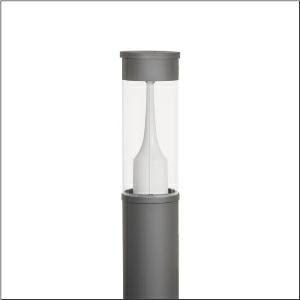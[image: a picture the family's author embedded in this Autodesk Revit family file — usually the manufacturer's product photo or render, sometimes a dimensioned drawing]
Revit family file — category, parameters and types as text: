
# Revit family: city-light_260_iq___p1_0a_5xa5295ff14h_c360
name_source: partatom
category: Lighting Fixtures
units: mm (PartAtom-declared; Revit-internal decimal feet)

## family parameters
Cut with Voids When Loaded = No
Host = Face
Light Source = No
Part Type = Normal
Room Calculation Point = No
Round Connector Dimension = Use Diameter
Shared = No

## types (1)
- --- (1 x LED, 1510 lm, 10.5 W, 3000K)
    Apparent Load = 11 VA
    CIE Flux Codes = 32 61 90 93 100
    Color Rendering = 70
    Color Temperature = 3000K
    Default Elevation = 1800 mm
    Description = City-Light 260 iQ, light pillar, Module 540 iQ-SR, primary light control with 3 zone facetted reflector, of plastic, silver coated, highly specular, structured, primary optical cover: cover, of PMMA, transparent, light distribution: P1.0a, primary light characteristic: strongly asymmetric, LED, High Power LED, rated luminous flux: 1.510lm, luminous efficacy: 144lm/W, light colour: 730, colour temperature: 3000K, control gear: ECG iQ, control: Auto-Match, Temp-Guard, Lumen-Switch, Night-Set, Smart-Wire, Light-Fading, Desk-Remote (wireless, voltage-free reading and setting of iQ features in the workshop via application-optimized NFC function/RFID function), optimised constant luminous flux control (CLO 2.0), Street-Remote, pre-setting: logarithmic dimming characteristic, with terminal, 6-pole, max. 2.5mm², mains connection: 230..240V, AC, 50/60Hz, start of lifetime: 11W, end of service life: 11W, reduction: 5W, luminaire housing, cylindrical, of extruded aluminium section, coated, Siteco® metallic grey (DB 702S), length: 2.600mm, diameter: 200mm, Module 540 iQ-SR, traffic white (RAL 9016), equipment: standard, protection rating (complete): IP65, insulation class (complete): insulation class II (safety insulation), certification: CE, ENEC, VDE, packaging unit: 1 piece

Light Distribution: P1.0a
    Height = 500 mm
    Lamp = 1 x LED
    Lamp Light Flux = 1510 lm
    Lamp Power = 10.5 W
    Lamp count = 1
    Length = 200 mm
    Luminous efficacy = 144 lm/W
    Manufacturer = Siteco
    ModVariant = No
    Model = 5XA5295FF14H
    Mounting Place = Floor
    Mounting Type = Freestanding
    Number of Poles = 1
    OnlyDefault = Yes
    Power Factor = 1
    Product Name = City-Light 260 iQ | P1.0a
    Product group = light pillar
    ProductGroupID = 1301
    Protection Class = Protection class II
    Protection Degree = IP 65
    RLX_Detail_Level = 1
    RLX_Emergency_Light_Flux = 0 lm
    RLX_Emergency_Type = 0
    RLX_Emergency_Type_DB = No
    RlxData = <blob elided: 52845 chars, md5=e8949f40>
    Socket = socket
    Standby Power = 0 W
    System Light Flux = 1510 lm
    System Power = 11 W
    Type Comments = factory setting: luminous flux: 100 % | dim-lin: 254 | 419 mA
    Type Image = l_1006918.jpg
    URL = http://relux.com
    VarID = @adj_129855
    Voltage = 0 V
    Weight = 0.00 kg
    Width = 0 mm  [stored 0 ft]

note: [stored X ft] marks values corroborated as IEEE doubles in the binary element streams (Revit-internal decimal feet)

## geometry (parser evidence)
native form markers: Blend x4, Sweep x12
no freeform markers — native parametric forms only
